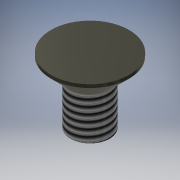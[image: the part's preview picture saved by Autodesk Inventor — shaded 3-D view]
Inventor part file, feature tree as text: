
AUTODESK INVENTOR PART (.ipt)
format: ipt  version: 2016 (Build 200138000, 138)  size: 129,536 bytes
history: native  units: mm
features: extrude x4, sketch x4, other x1, thread x1, chamfer x1
ambient origin geometry x1: Origin
bodies: Body1 (feature_tree)
feature tree (11):
  other  "ソリッド1"
  extrude  "押し出し1"  Depth=3.0mm
  extrude  "押し出し2"  Depth=6.0mm TaperAngle=0.0deg
  thread  "ねじ1"
  chamfer  "面取り1"  Distance=6.0mm
  extrude  "押し出し4"  Depth=1.75mm TaperAngle=0.0deg
  extrude  "押し出し5"  Depth=10.0mm TaperAngle=0.0deg
  sketch  "スケッチ1"
  sketch  "スケッチ2"
  sketch  "スケッチ4"
  sketch  "スケッチ5"
